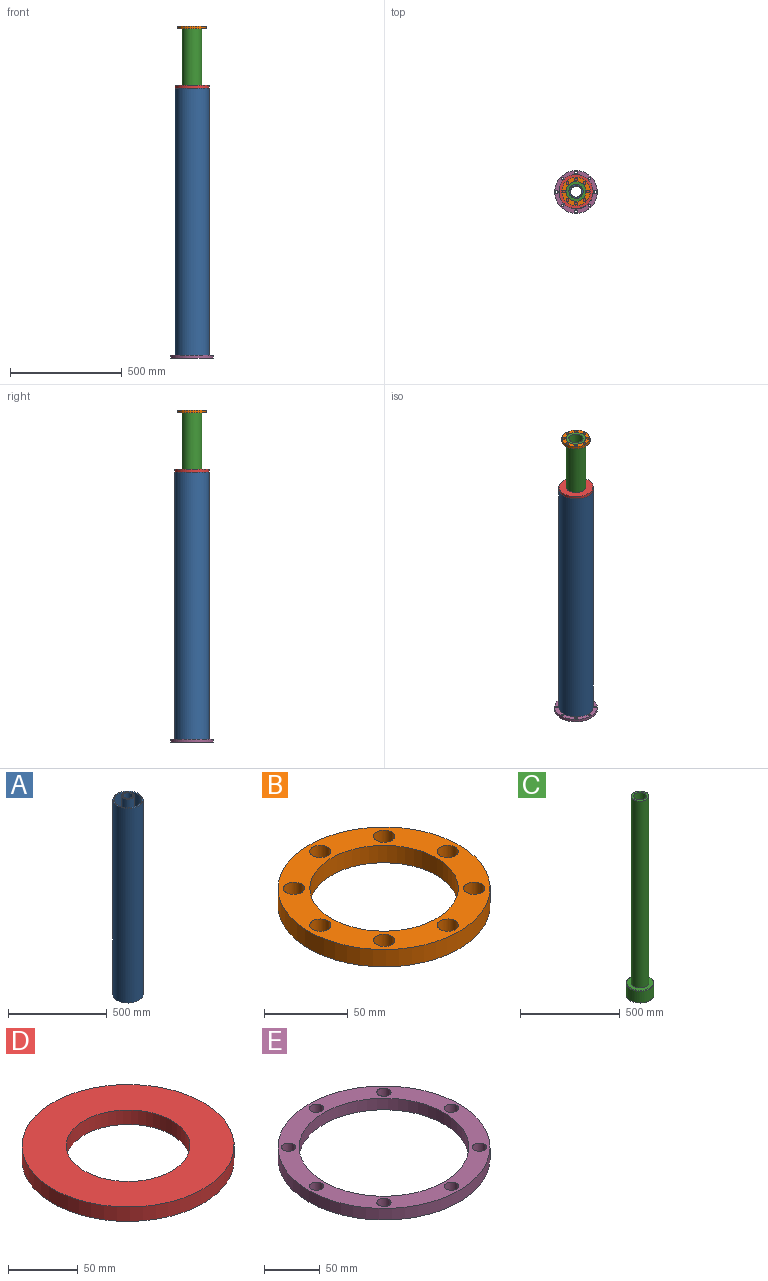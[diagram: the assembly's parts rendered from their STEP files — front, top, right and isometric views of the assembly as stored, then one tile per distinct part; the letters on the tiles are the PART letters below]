
ASSEMBLY  parts=5 mates=4
PART A: 8 faces, bbox 152.4x152.4x1231.9 mm
  f0: cylinder r=25.4mm len=1231.9mm, axis (0,0,-1), area 196602.5mm2, adj f3,f7
  f1: cylinder r=76.2mm len=1206.5mm, axis (0,0,-1), area 577646.5mm2, adj f2,f3
  f2: plane 152.4x152.4mm, normal (0,0,1), area 2913.6mm2, adj f1,f5
  f3: plane 152.4x152.4mm, normal (0,0,-1), area 16214.6mm2, adj f0,f1
  f4: cylinder r=31.75mm len=1219.2mm, axis (0,0,1), area 243219.6mm2, adj f6,f7
  f5: cylinder r=69.85mm len=1193.8mm, axis (0,0,1), area 523935.5mm2, adj f2,f6
  f6: plane 139.7x139.7mm, normal (0,0,1), area 12161mm2, adj f4,f5
  f7: plane 63.5x63.5mm, normal (0,0,1), area 1140.1mm2, adj f0,f4
PART B: 12 faces, bbox 127x127x12.7 mm
  f0: cylinder r=6.35mm len=12.7mm, axis (0,0,1), area 506.7mm2, adj f10,f11
  f1: cylinder r=6.35mm len=12.7mm, axis (0,0,1), area 506.7mm2, adj f10,f11
  f2: cylinder r=6.35mm len=12.7mm, axis (0,0,1), area 506.7mm2, adj f10,f11
  f3: cylinder r=6.35mm len=12.7mm, axis (0,0,1), area 506.7mm2, adj f10,f11
  f4: cylinder r=6.35mm len=12.7mm, axis (0,0,1), area 506.7mm2, adj f10,f11
  f5: cylinder r=6.35mm len=12.7mm, axis (0,0,1), area 506.7mm2, adj f10,f11
  f6: cylinder r=6.35mm len=12.7mm, axis (0,0,1), area 506.7mm2, adj f10,f11
  f7: cylinder r=6.35mm len=12.7mm, axis (0,0,1), area 506.7mm2, adj f10,f11
  f8: cylinder r=44.45mm len=88.9mm, axis (0,0,1), area 3547mm2, adj f10,f11
  f9: cylinder r=63.5mm len=127mm, axis (0,0,1), area 5067.1mm2, adj f10,f11
  f10: plane 127x127mm, normal (0,0,-1), area 5447.1mm2, adj f0,f1,f2,f3,f4,f5,f6,f7
  f11: plane 127x127mm, normal (0,0,1), area 5447.1mm2, adj f0,f1,f2,f3,f4,f5,f6,f7
PART C: 8 faces, bbox 151.2x151.2x1219.2 mm
  f0: cylinder r=31.75mm len=1219.2mm, axis (0,0,-1), area 243219.6mm2, adj f3,f5
  f1: cylinder r=69.85mm len=139.7mm, axis (0,0,-1), area 30655.8mm2, adj f6,f7
  f2: plane 133.35x133.35mm, normal (0,0,1), area 7759mm2, adj f4,f7
  f3: plane 133.35x133.35mm, normal (0,0,-1), area 10799.2mm2, adj f0,f6
  f4: cylinder r=44.45mm len=1143mm, axis (0,0,-1), area 319225.7mm2, adj f2,f5
  f5: plane 88.9x88.9mm, normal (0,0,1), area 3040.2mm2, adj f0,f4
  f6: torus R=66.67mm, axis (0,0,1), area 2152.7mm2, adj f1,f3
  f7: torus R=66.67mm, axis (0,0,1), area 2152.7mm2, adj f1,f2
PART D: 4 faces, bbox 152.4x152.4x12.7 mm
  f0: cylinder r=44.45mm len=88.9mm, axis (0,0,-1), area 3547mm2, adj f2,f3
  f1: cylinder r=76.2mm len=152.4mm, axis (0,0,-1), area 6080.5mm2, adj f2,f3
  f2: plane 152.4x152.4mm, normal (0,0,1), area 12034.3mm2, adj f0,f1
  f3: plane 152.4x152.4mm, normal (0,0,-1), area 12034.3mm2, adj f0,f1
PART E: 12 faces, bbox 190.5x190.5x12.7 mm
  f0: cylinder r=6.35mm len=12.7mm, axis (0,0,-1), area 506.7mm2, adj f10,f11
  f1: cylinder r=6.35mm len=12.7mm, axis (0,0,-1), area 506.7mm2, adj f10,f11
  f2: cylinder r=6.35mm len=12.7mm, axis (0,0,-1), area 506.7mm2, adj f10,f11
  f3: cylinder r=6.35mm len=12.7mm, axis (0,0,-1), area 506.7mm2, adj f10,f11
  f4: cylinder r=6.35mm len=12.7mm, axis (0,0,-1), area 506.7mm2, adj f10,f11
  f5: cylinder r=6.35mm len=12.7mm, axis (0,0,-1), area 506.7mm2, adj f10,f11
  f6: cylinder r=6.35mm len=12.7mm, axis (0,0,-1), area 506.7mm2, adj f10,f11
  f7: cylinder r=6.35mm len=12.7mm, axis (0,0,-1), area 506.7mm2, adj f10,f11
  f8: cylinder r=76.2mm len=152.4mm, axis (0,0,-1), area 6080.5mm2, adj f10,f11
  f9: cylinder r=95.25mm len=190.5mm, axis (0,0,-1), area 7600.6mm2, adj f10,f11
  f10: plane 190.5x190.5mm, normal (0,0,1), area 9247.4mm2, adj f0,f1,f2,f3,f4,f5,f6,f7
  f11: plane 190.5x190.5mm, normal (0,0,-1), area 9247.4mm2, adj f0,f1,f2,f3,f4,f5,f6,f7
PLACE A at identity
PLACE B rot(axis=(1,0,0),180deg) t=(0,0,2690.76)mm
PLACE C t=(0,0,265.06)mm
PLACE D t=(0,0,1206.5)mm
PLACE E rot(axis=(1,0,0),180deg) t=(0,0,12.7)mm
MATE slider C.f4 <-> D.f1  axis (0,0,-1) through (0,0,265.06)mm
MATE fastened D.f1 <-> A.f1  axis (0,0,-1) through (0,0,1206.5)mm
MATE fastened B.f9 <-> C.f4  axis (0,0,1) through (0,0,1484.26)mm
MATE fastened E.f9 <-> A.f1  axis (0,0,-1) through (0,0,0)mm
